# Revit family: 210_CAD O Integral EC 07 VLEXG
name_source: partatom
category: Mechanical Equipment
units: mm (PartAtom-declared; Revit-internal decimal feet)

## family parameters
Always vertical = Yes
Cut with Voids When Loaded = No
Part Type = Breaks Into
Room Calculation Point = No
Round Connector Dimension = Use Diameter
Shared = No
Work Plane-Based = No

## types (1)
- CAD O Integral EC 07 VLEXG
    AA1 = 655 mm
    AA2 = 655 mm
    AA3 = 58 mm  [stored 0.190289 ft]
    AA3__ve = -58 mm  [stored -0.190289 ft]
    AA4 = 713 mm
    BB1 = 358 mm  [stored 1.17454 ft]
    CAT0 = Yes
    D = 315 mm
    HH1 = 983 mm  [stored 3.22507 ft]
    Manufacturer = VIM
    QmdConnectorList = 221;D;231;D;241;D;251;D
    R = 158 mm
    SPG = 329 mm  [stored 1.0794 ft]
    SPH = 754 mm  [stored 2.47375 ft]
    SPI1 = 328 mm  [stored 1.07612 ft]
    SPI2 = 358 mm  [stored 1.17454 ft]
    SPN = 1568 mm  [stored 5.14436 ft]
    SPR = 85 mm  [stored 0.278871 ft]
    SPS = 54 mm  [stored 0.177165 ft]
    SS1 = 450 mm  [stored 1.47638 ft]
    SS2 = 784 mm  [stored 2.57218 ft]
    W = 500 mm
    magiPartTypeId = 210
    magiProductCode = CAD O Integral EC 07 VLEXG
    magiProductFamilyId = CAD O Integral EC 07 VLEXG
    magiProductId = CAD O Integral EC 07 VLEXG

note: [stored X ft] marks values corroborated as IEEE doubles in the binary element streams (Revit-internal decimal feet)

## geometry (parser evidence)
native form markers: Sweep x2
no freeform markers — native parametric forms only
